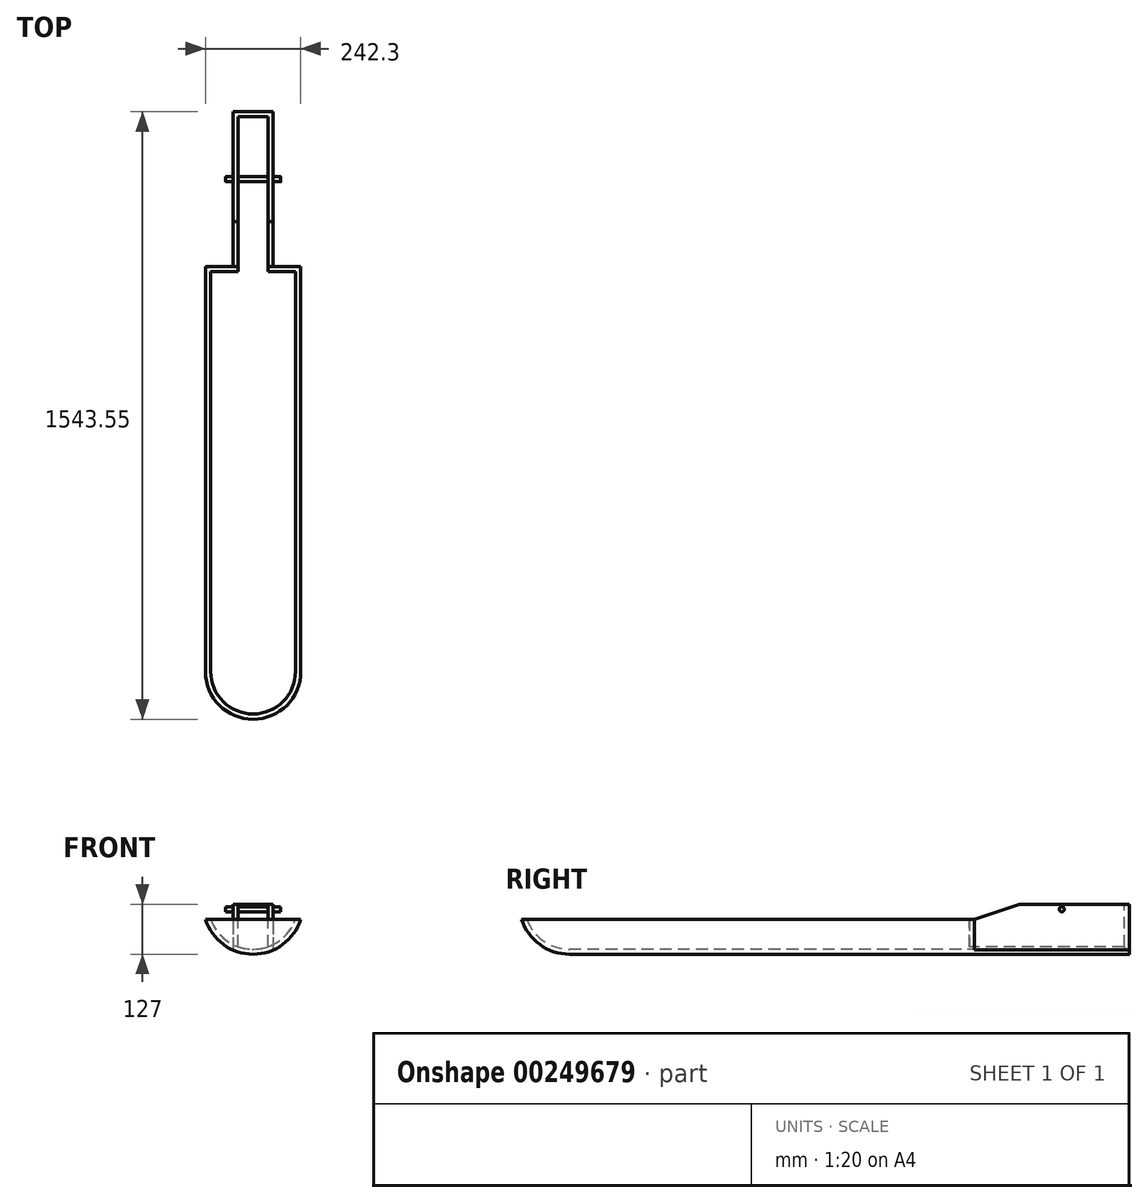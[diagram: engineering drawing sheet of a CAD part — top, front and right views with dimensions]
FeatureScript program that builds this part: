
annotation { "Feature Type Name" : "Feature", "Feature Type Description" : "" }
export const myFeature = defineFeature(function(context is Context, id is Id, definition is map)
    precondition{}
    {
        {
            var Q0;
            Q0=qCreatedBy(makeId("Right.planeOp"),FACE);
            var sketch = newSketch(context, id + "F0", { "sketchPlane" : qUnion([Q0])});
            skArc(sketch, "E0", {"start": v(-635, 0) * mm, "mid": v(-597.8, -89.8) * mm, "end": v(-508, -127) * mm});
            skArc(sketch, "E1", {"start": v(-622.3, 0) * mm, "mid": v(-588.82, -80.82) * mm, "end": v(-508, -114.3) * mm});
            skLineSegment(sketch, "E2.trimOffspring", {"start": v(-622.3, 0) * mm, "end": v(-635, 0) * mm});
            skLineSegment(sketch, "E3", {"start": v(-508, -114.3) * mm, "end": v(-508, -127) * mm});
            skSolve(sketch);
        }
        {
            var Q0;
            Q0=makeQuery(id+"F0.imprint","IMPRINT",FACE,{"disambiguationData":[TD([[makeQuery(id+"F0.imprint","IMPRINT",EDGE,{"derivedFrom":sQuery(id+"F0.wireOp",EDGE,"E0")}),1.0]])]});
            var Q1;
            Q1=sQuery(id+"F0.wireOp",EDGE,"E2.trimOffspring");
            revolve(context, id + "F1", {"entities" : qUnion([Q0]), "axis" : qUnion([Q1]), "revolveType" : RevolveType.SYMMETRIC, "angle" : 180 * degree});
        }
        {
            var Q0;
            Q0=makeQuery(id+"F1.opRevolve","SWEPT_FACE",FACE,{"disambiguationData":[OSD([sQuery(id+"F0.wireOp",EDGE,"E3")])]});
            var sketch = newSketch(context, id + "F2", { "sketchPlane" : qUnion([Q0])});
            skArc(sketch, "E4", {"start": v(-127, 0) * mm, "mid": v(0, -127) * mm, "end": v(127, 0) * mm});
            skArc(sketch, "E5", {"start": v(-114.3, 0) * mm, "mid": v(0, -114.3) * mm, "end": v(114.3, 0) * mm});
            skLineSegment(sketch, "E6", {"start": v(-127, 0) * mm, "end": v(-114.3, 0) * mm});
            skLineSegment(sketch, "E7", {"start": v(114.3, 0) * mm, "end": v(127, 0) * mm});
            skSolve(sketch);
        }
        {
            var Q0;
            Q0 = qSketchRegion(id + "F2", true);
            extrude(context, id + "F3", {"entities" : qUnion([Q0]), "operationType" : NewBodyOperationType.ADD, "depth" : 1016 * mm});
        }
        {
            var Q0;
            Q0=makeQuery(id+"F3.opExtrude","CAP_FACE",FACE,{"disambiguationData":[OSD([sQuery(id+"F2.wireOp",EDGE,"E4"),sQuery(id+"F2.wireOp",EDGE,"E5"),sQuery(id+"F2.wireOp",EDGE,"E6"),sQuery(id+"F2.wireOp",EDGE,"E7")])],"isStart":false});
            var sketch = newSketch(context, id + "F4", { "sketchPlane" : qUnion([Q0])});
            skArc(sketch, "E8", {"start": v(-127, 0) * mm, "mid": v(0, -127) * mm, "end": v(127, 0) * mm});
            skArc(sketch, "E9", {"start": v(-38.1, -107.76) * mm, "mid": v(0, -114.3) * mm, "end": v(38.1, -107.76) * mm});
            skLineSegment(sketch, "E10", {"start": v(-38.1, -107.76) * mm, "end": v(-38.1, 0) * mm});
            skLineSegment(sketch, "E11", {"start": v(38.1, -107.76) * mm, "end": v(38.1, 0) * mm});
            skLineSegment(sketch, "E12", {"start": v(-38.1, 0) * mm, "end": v(-127, 0) * mm});
            skLineSegment(sketch, "E13", {"start": v(38.1, 0) * mm, "end": v(127, 0) * mm});
            skSolve(sketch);
        }
        {
            var Q0;
            Q0 = qSketchRegion(id + "F4", true);
            extrude(context, id + "F5", {"entities" : qUnion([Q0]), "operationType" : NewBodyOperationType.ADD, "depth" : 12.7 * mm});
        }
        {
            var Q0;
            Q0=makeQuery(id+"F5.opExtrude","CAP_FACE",FACE,{"disambiguationData":[OSD([sQuery(id+"F4.wireOp",EDGE,"E8"),sQuery(id+"F4.wireOp",EDGE,"E9"),sQuery(id+"F4.wireOp",EDGE,"E10"),sQuery(id+"F4.wireOp",EDGE,"E11"),sQuery(id+"F4.wireOp",EDGE,"E12"),sQuery(id+"F4.wireOp",EDGE,"E13")])],"isStart":false});
            var sketch = newSketch(context, id + "F6", { "sketchPlane" : qUnion([Q0])});
            skLineSegment(sketch, "E14", {"start": v(-50.8, 0) * mm, "end": v(-50.8, -116.4) * mm});
            skLineSegment(sketch, "E15", {"start": v(50.8, 0) * mm, "end": v(50.8, -116.4) * mm});
            skLineSegment(sketch, "E16", {"start": v(-50.8, 0) * mm, "end": v(-38.1, 0) * mm});
            skLineSegment(sketch, "E17", {"start": v(-38.1, 0) * mm, "end": v(-38.1, -107.76) * mm});
            skLineSegment(sketch, "E18", {"start": v(50.8, 0) * mm, "end": v(38.1, 0) * mm});
            skLineSegment(sketch, "E19", {"start": v(38.1, 0) * mm, "end": v(38.1, -107.76) * mm});
            skArc(sketch, "E20", {"start": v(-50.8, -116.4) * mm, "mid": v(0, -127) * mm, "end": v(50.8, -116.4) * mm});
            skArc(sketch, "E21", {"start": v(-38.1, -107.76) * mm, "mid": v(0, -114.3) * mm, "end": v(38.1, -107.76) * mm});
            skSolve(sketch);
        }
        {
            var Q0;
            Q0=makeQuery(id+"F6.imprint","IMPRINT",FACE,{"disambiguationData":[TD([[makeQuery(id+"F6.imprint","IMPRINT",EDGE,{"derivedFrom":sQuery(id+"F6.wireOp",EDGE,"E14")}),1.0]])]});
            extrude(context, id + "F7", {"entities" : qUnion([Q0]), "operationType" : NewBodyOperationType.ADD, "depth" : 381 * mm});
        }
        {
            var Q0;
            Q0=makeQuery(id+"F7.opExtrude","CAP_FACE",FACE,{"disambiguationData":[OSD([sQuery(id+"F6.wireOp",EDGE,"E14"),sQuery(id+"F6.wireOp",EDGE,"E15"),sQuery(id+"F6.wireOp",EDGE,"E16"),sQuery(id+"F6.wireOp",EDGE,"E17"),sQuery(id+"F6.wireOp",EDGE,"E18"),sQuery(id+"F6.wireOp",EDGE,"E19"),sQuery(id+"F6.wireOp",EDGE,"E20"),sQuery(id+"F6.wireOp",EDGE,"E21")])],"isStart":false});
            var sketch = newSketch(context, id + "F8", { "sketchPlane" : qUnion([Q0])});
            skArc(sketch, "E22", {"start": v(-50.8, -116.4) * mm, "mid": v(0, -127) * mm, "end": v(50.8, -116.4) * mm});
            skLineSegment(sketch, "E23", {"start": v(-50.8, 0) * mm, "end": v(50.8, 0) * mm});
            skLineSegment(sketch, "E24", {"start": v(50.8, 0) * mm, "end": v(50.8, -116.4) * mm});
            skLineSegment(sketch, "E25", {"start": v(-50.8, 0) * mm, "end": v(-50.8, -116.4) * mm});
            skSolve(sketch);
        }
        {
            var Q0;
            Q0 = qSketchRegion(id + "F8", true);
            extrude(context, id + "F9", {"entities" : qUnion([Q0]), "operationType" : NewBodyOperationType.ADD, "depth" : 12.7 * mm});
        }
        {
            var Q0;
            Q0=qCreatedBy(makeId("Right.planeOp"),FACE);
            var sketch = newSketch(context, id + "F10", { "sketchPlane" : qUnion([Q0])});
            skLineSegment(sketch, "E26", {"start": v(-635, 0) * mm, "end": v(635, 0) * mm});
            skLineSegment(sketch, "E27", {"start": v(635, 0) * mm, "end": v(520.7, -38.1) * mm});
            skLineSegment(sketch, "E28", {"start": v(520.7, -38.1) * mm, "end": v(-629.15, -38.1) * mm});
            skArc(sketch, "E29", {"start": v(-635, 0) * mm, "mid": v(-633.53, -19.27) * mm, "end": v(-629.15, -38.1) * mm});
            skSolve(sketch);
        }
        {
            var Q0;
            Q0 = qSketchRegion(id + "F10", true);
            extrude(context, id + "F11", {"entities" : qUnion([Q0]), "operationType" : NewBodyOperationType.REMOVE, "endBound" : BoundingType.SYMMETRIC, "oppositeDirection" : true, "depth" : 254 * mm});
        }
        {
            var Q0;
            Q0=qCreatedBy(makeId("Right.planeOp"),FACE);
            var sketch = newSketch(context, id + "F12", { "sketchPlane" : qUnion([Q0])});
            skCircle(sketch, "E30", {"center": v(742.95, -12.7) * mm, "radius": 6.35 * mm});
            skSolve(sketch);
        }
        {
            var Q0;
            Q0 = qSketchRegion(id + "F12", true);
            extrude(context, id + "F13", {"entities" : qUnion([Q0]), "operationType" : NewBodyOperationType.ADD, "endBound" : BoundingType.SYMMETRIC, "depth" : 139.7 * mm});
        }
    });
